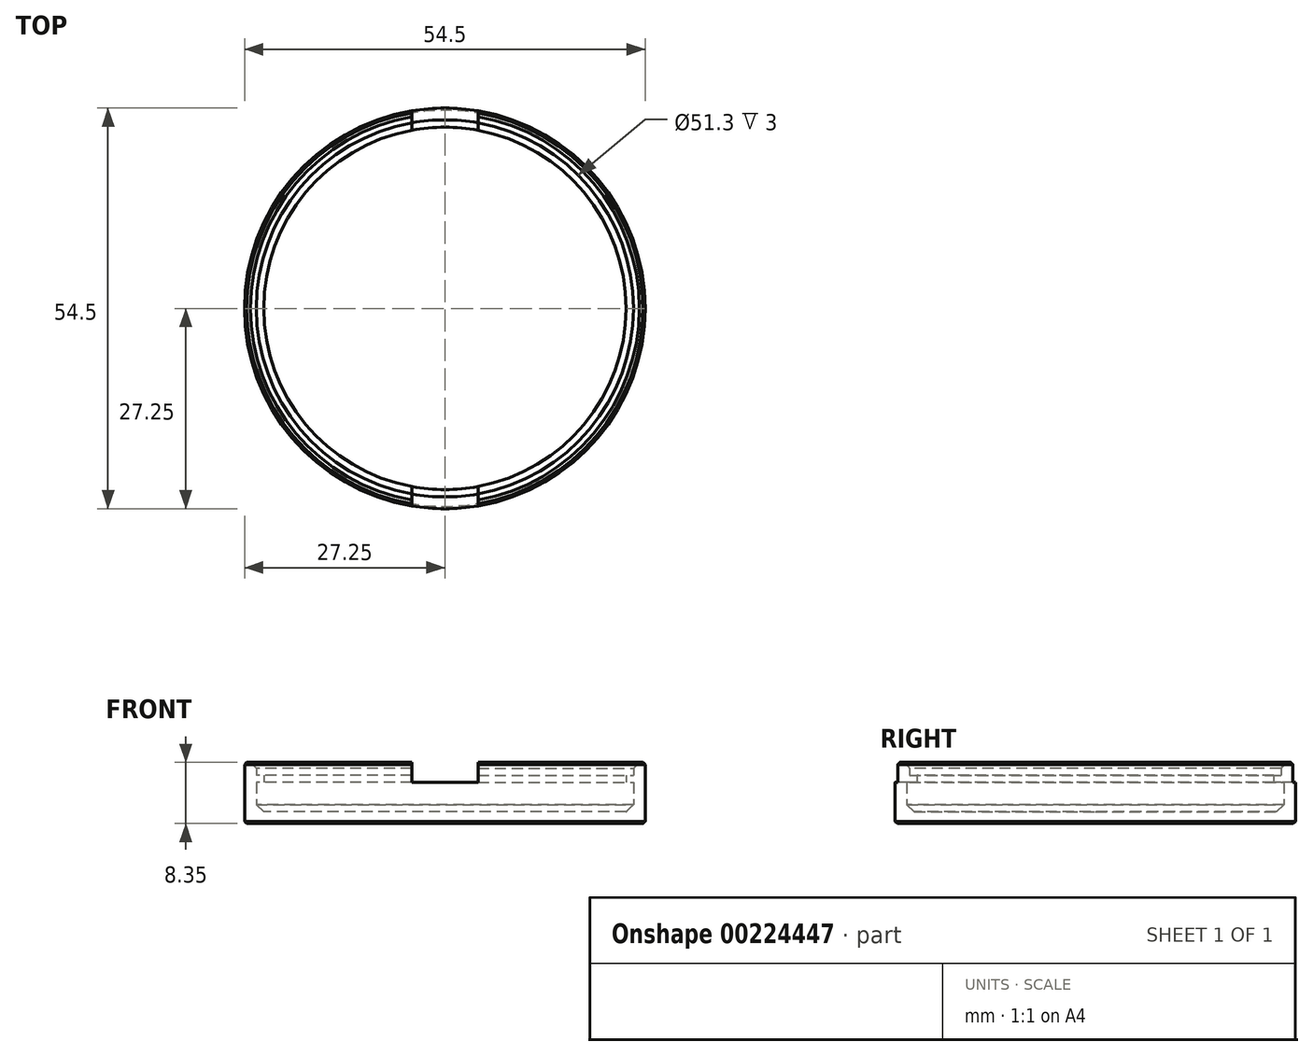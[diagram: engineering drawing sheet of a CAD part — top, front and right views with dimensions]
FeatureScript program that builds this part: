
annotation { "Feature Type Name" : "Feature", "Feature Type Description" : "" }
export const myFeature = defineFeature(function(context is Context, id is Id, definition is map)
    precondition{}
    {
        {
            assignVariable(context, id + "F0", {"name" : "_Tolerance", "anyValue" : .3});
        }
        {
            assignVariable(context, id + "F1", {"name" : "BatteryThickness", "anyValue" : 4});
        }
        {
            assignVariable(context, id + "F2", {"name" : "CPThickness", "anyValue" : 1.75});
        }
        {
            assignVariable(context, id + "F3", {"name" : "LipDepth", "anyValue" : 1});
        }
        {
            assignVariable(context, id + "F4", {"name" : "WallThickness", "anyValue" : 1.6});
        }
        {
            var Q0;
            Q0=qCreatedBy(makeId("Top.planeOp"),FACE);
            var sketch = newSketch(context, id + "F5", { "sketchPlane" : qUnion([Q0])});
            skCircle(sketch, "E0", {"center": v(0, 0) * mm, "radius": 25.65 * mm});
            skLineSegment(sketch, "E1", {"start": v(0, 25.65) * mm, "end": v(0, -25.65) * mm, "construction": true});
            skCircle(sketch, "E2.0", {"center": v(0, 0) * mm, "radius": 27.25 * mm});
            skCircle(sketch, "E3.0", {"center": v(0, 0) * mm, "radius": 24.65 * mm});
            skLineSegment(sketch, "E4", {"start": v(-4.5, 26.88) * mm, "end": v(-4.5, 24.24) * mm});
            skLineSegment(sketch, "E5.MirrorCS", {"start": v(4.5, 26.88) * mm, "end": v(4.5, 24.24) * mm});
            skLineSegment(sketch, "E6.trimOffspring", {"start": v(-4.5, -24.24) * mm, "end": v(-4.5, -26.88) * mm});
            skLineSegment(sketch, "E7.trimOffspring", {"start": v(4.5, -24.24) * mm, "end": v(4.5, -26.88) * mm});
            skSolve(sketch);
        }
        {
            var Q0;
            {var subQ0=sQuery(id+"F5.wireOp",EDGE,"E3.0");var subQ1=makeQuery(id+"F5.imprint","INTERSECT",VERTEX,{"derivedFrom":[subQ0,sQuery(id+"F5.wireOp",EDGE,"E4")]});Q0=makeQuery(id+"F5.imprint","IMPRINT",FACE,{"disambiguationData":[TD([[makeQuery(id+"F5.imprint","IMPRINT",EDGE,{"disambiguationData":[TD([[subQ1,1.0]])],"derivedFrom":subQ0}),1.0]])]});}
            extrude(context, id + "F6", {"entities" : qUnion([Q0]), "depth" : (getVariable(context, 'WallThickness') + getVariable(context, 'BatteryThickness')) * mm});
        }
        {
            var Q0;
            {var subQ0=sQuery(id+"F5.wireOp",EDGE,"E4");var subQ1=sQuery(id+"F5.wireOp",EDGE,"E0");var subQ2=makeQuery(id+"F5.imprint","INTERSECT",VERTEX,{"derivedFrom":[subQ1,subQ0]});Q0=makeQuery(id+"F5.imprint","IMPRINT",FACE,{"disambiguationData":[TD([[makeQuery(id+"F5.imprint","IMPRINT",EDGE,{"disambiguationData":[TD([[subQ2,-1.0]])],"derivedFrom":subQ1}),1.0]])]});}
            var Q1;
            {var subQ0=sQuery(id+"F5.wireOp",EDGE,"E6.trimOffspring");var subQ1=sQuery(id+"F5.wireOp",EDGE,"E0");var subQ2=makeQuery(id+"F5.imprint","INTERSECT",VERTEX,{"derivedFrom":[subQ1,subQ0]});Q1=makeQuery(id+"F5.imprint","IMPRINT",FACE,{"disambiguationData":[TD([[makeQuery(id+"F5.imprint","IMPRINT",EDGE,{"disambiguationData":[TD([[subQ2,-1.0]])],"derivedFrom":subQ1}),1.0]])]});}
            var Q2;
            {var subQ0=sQuery(id+"F5.wireOp",EDGE,"E5.MirrorCS");var subQ1=sQuery(id+"F5.wireOp",EDGE,"E0");var subQ2=makeQuery(id+"F5.imprint","INTERSECT",VERTEX,{"derivedFrom":[subQ1,subQ0]});Q2=makeQuery(id+"F5.imprint","IMPRINT",FACE,{"disambiguationData":[TD([[makeQuery(id+"F5.imprint","IMPRINT",EDGE,{"disambiguationData":[TD([[subQ2,1.0]])],"derivedFrom":subQ1}),1.0]])]});}
            var Q3;
            {var subQ0=sQuery(id+"F5.wireOp",EDGE,"E4");var subQ1=sQuery(id+"F5.wireOp",EDGE,"E0");var subQ2=makeQuery(id+"F5.imprint","INTERSECT",VERTEX,{"derivedFrom":[subQ1,subQ0]});Q3=makeQuery(id+"F5.imprint","IMPRINT",FACE,{"disambiguationData":[TD([[makeQuery(id+"F5.imprint","IMPRINT",EDGE,{"disambiguationData":[TD([[subQ2,1.0]])],"derivedFrom":subQ1}),1.0]])]});}
            extrude(context, id + "F7", {"entities" : qUnion([Q0, Q1, Q2, Q3]), "operationType" : NewBodyOperationType.ADD, "depth" : (getVariable(context, 'WallThickness') + getVariable(context, 'BatteryThickness') + getVariable(context, 'LipDepth')) * mm});
        }
        {
            var Q0;
            {var subQ0=sQuery(id+"F5.wireOp",EDGE,"E4");var subQ1=sQuery(id+"F5.wireOp",EDGE,"E0");var subQ2=makeQuery(id+"F5.imprint","INTERSECT",VERTEX,{"derivedFrom":[subQ1,subQ0]});Q0=makeQuery(id+"F5.imprint","IMPRINT",FACE,{"disambiguationData":[TD([[makeQuery(id+"F5.imprint","IMPRINT",EDGE,{"disambiguationData":[TD([[subQ2,-1.0]])],"derivedFrom":subQ1}),-1.0]])]});}
            var Q1;
            {var subQ0=sQuery(id+"F5.wireOp",EDGE,"E6.trimOffspring");var subQ1=sQuery(id+"F5.wireOp",EDGE,"E0");var subQ2=makeQuery(id+"F5.imprint","INTERSECT",VERTEX,{"derivedFrom":[subQ1,subQ0]});Q1=makeQuery(id+"F5.imprint","IMPRINT",FACE,{"disambiguationData":[TD([[makeQuery(id+"F5.imprint","IMPRINT",EDGE,{"disambiguationData":[TD([[subQ2,-1.0]])],"derivedFrom":subQ1}),-1.0]])]});}
            var Q2;
            {var subQ0=sQuery(id+"F5.wireOp",EDGE,"E5.MirrorCS");var subQ1=sQuery(id+"F5.wireOp",EDGE,"E0");var subQ2=makeQuery(id+"F5.imprint","INTERSECT",VERTEX,{"derivedFrom":[subQ1,subQ0]});Q2=makeQuery(id+"F5.imprint","IMPRINT",FACE,{"disambiguationData":[TD([[makeQuery(id+"F5.imprint","IMPRINT",EDGE,{"disambiguationData":[TD([[subQ2,1.0]])],"derivedFrom":subQ1}),-1.0]])]});}
            var Q3;
            {var subQ0=sQuery(id+"F5.wireOp",EDGE,"E4");var subQ1=sQuery(id+"F5.wireOp",EDGE,"E0");var subQ2=makeQuery(id+"F5.imprint","INTERSECT",VERTEX,{"derivedFrom":[subQ1,subQ0]});Q3=makeQuery(id+"F5.imprint","IMPRINT",FACE,{"disambiguationData":[TD([[makeQuery(id+"F5.imprint","IMPRINT",EDGE,{"disambiguationData":[TD([[subQ2,1.0]])],"derivedFrom":subQ1}),-1.0]])]});}
            extrude(context, id + "F8", {"entities" : qUnion([Q0, Q1, Q2, Q3]), "operationType" : NewBodyOperationType.ADD, "depth" : (getVariable(context, 'WallThickness') + getVariable(context, 'BatteryThickness') + getVariable(context, 'LipDepth') + getVariable(context, 'CPThickness')) * mm});
        }
        {
            var Q0;
            {var subQ0=sQuery(id+"F5.wireOp",EDGE,"E6.trimOffspring");var subQ1=sQuery(id+"F5.wireOp",EDGE,"E0");var subQ2=makeQuery(id+"F5.imprint","INTERSECT",VERTEX,{"derivedFrom":[subQ1,subQ0]});Q0=makeQuery(id+"F5.imprint","IMPRINT",FACE,{"disambiguationData":[TD([[makeQuery(id+"F5.imprint","IMPRINT",EDGE,{"disambiguationData":[TD([[subQ2,-1.0]])],"derivedFrom":subQ1}),-1.0]])]});}
            var Q1;
            {var subQ0=sQuery(id+"F5.wireOp",EDGE,"E5.MirrorCS");var subQ1=sQuery(id+"F5.wireOp",EDGE,"E0");var subQ2=makeQuery(id+"F5.imprint","INTERSECT",VERTEX,{"derivedFrom":[subQ1,subQ0]});Q1=makeQuery(id+"F5.imprint","IMPRINT",FACE,{"disambiguationData":[TD([[makeQuery(id+"F5.imprint","IMPRINT",EDGE,{"disambiguationData":[TD([[subQ2,-1.0]])],"derivedFrom":subQ1}),-1.0]])]});}
            var Q2;
            {var subQ0=sQuery(id+"F5.wireOp",EDGE,"E6.trimOffspring");var subQ1=sQuery(id+"F5.wireOp",EDGE,"E0");var subQ2=makeQuery(id+"F5.imprint","INTERSECT",VERTEX,{"derivedFrom":[subQ1,subQ0]});Q2=makeQuery(id+"F5.imprint","IMPRINT",FACE,{"disambiguationData":[TD([[makeQuery(id+"F5.imprint","IMPRINT",EDGE,{"disambiguationData":[TD([[subQ2,-1.0]])],"derivedFrom":subQ1}),1.0]])]});}
            var Q3;
            {var subQ0=sQuery(id+"F5.wireOp",EDGE,"E4");var subQ1=sQuery(id+"F5.wireOp",EDGE,"E0");var subQ2=makeQuery(id+"F5.imprint","INTERSECT",VERTEX,{"derivedFrom":[subQ1,subQ0]});Q3=makeQuery(id+"F5.imprint","IMPRINT",FACE,{"disambiguationData":[TD([[makeQuery(id+"F5.imprint","IMPRINT",EDGE,{"disambiguationData":[TD([[subQ2,1.0]])],"derivedFrom":subQ1}),1.0]])]});}
            extrude(context, id + "F9", {"entities" : qUnion([Q0, Q1, Q2, Q3]), "operationType" : NewBodyOperationType.REMOVE, "depth" : (getVariable(context, 'WallThickness') + getVariable(context, 'BatteryThickness') + getVariable(context, 'LipDepth') + getVariable(context, 'CPThickness')) * mm, "hasSecondDirection" : true, "secondDirectionOppositeDirection" : false, "secondDirectionDepth" : (getVariable(context, 'WallThickness') + getVariable(context, 'BatteryThickness')) * mm});
        }
        {
            var Q0;
            {var subQ0=sQuery(id+"F5.wireOp",EDGE,"E3.0");var subQ1=sQuery(id+"F5.wireOp",EDGE,"E2.0");Q0=makeQuery(id+"F9.boolean.opBoolean","MERGE",FACE,{"derivedFrom":[makeQuery(id+"F6.opExtrude","CAP_FACE",FACE,{"disambiguationData":[OSD([subQ0])],"isStart":false}),makeQuery(id+"F9.opExtrude","CAP_FACE",FACE,{"disambiguationData":[OSD([subQ1,subQ0,sQuery(id+"F5.wireOp",EDGE,"E4"),sQuery(id+"F5.wireOp",EDGE,"E5.MirrorCS")])],"isStart":true}),makeQuery(id+"F9.opExtrude","CAP_FACE",FACE,{"disambiguationData":[OSD([subQ1,subQ0,sQuery(id+"F5.wireOp",EDGE,"E6.trimOffspring"),sQuery(id+"F5.wireOp",EDGE,"E7.trimOffspring")])],"isStart":true})]});}
            shell(context, id + "F10", {"entities" : qUnion([Q0]), "thickness" : (getVariable(context, 'WallThickness')) * mm});
        }
        {
            var Q0;
            {var subQ0=sQuery(id+"F5.wireOp",EDGE,"E2.0");Q0=makeQuery(id+"F10.opShell","OFFSET_EDGE",EDGE,{"disambiguationData":[OSD([subQ0]),TDD([makeQuery(id+"F9.boolean.opBoolean","COPY",EDGE,{"derivedFrom":makeQuery(id+"F9.opExtrude","CAP_EDGE",EDGE,{"disambiguationData":[OSD([subQ0]),TDD([makeQuery(id+"F5.imprint","IMPRINT",EDGE,{"disambiguationData":[TD([[makeQuery(id+"F5.imprint","INTERSECT",VERTEX,{"derivedFrom":[subQ0,sQuery(id+"F5.wireOp",EDGE,"E4")]}),1.0]])],"derivedFrom":subQ0})])],"isStart":true})}),makeQuery(id+"F9.boolean.opBoolean","COPY",EDGE,{"derivedFrom":makeQuery(id+"F9.opExtrude","CAP_EDGE",EDGE,{"disambiguationData":[OSD([subQ0]),TDD([makeQuery(id+"F5.imprint","IMPRINT",EDGE,{"disambiguationData":[TD([[makeQuery(id+"F5.imprint","INTERSECT",VERTEX,{"derivedFrom":[subQ0,sQuery(id+"F5.wireOp",EDGE,"E6.trimOffspring")]}),-1.0]])],"derivedFrom":subQ0})])],"isStart":true})})]),OD(2.0)]});}
            var Q1;
            {var subQ0=sQuery(id+"F5.wireOp",EDGE,"E2.0");Q1=makeQuery(id+"F10.opShell","OFFSET_EDGE",EDGE,{"disambiguationData":[OSD([subQ0]),TDD([makeQuery(id+"F9.boolean.opBoolean","COPY",EDGE,{"derivedFrom":makeQuery(id+"F9.opExtrude","CAP_EDGE",EDGE,{"disambiguationData":[OSD([subQ0]),TDD([makeQuery(id+"F5.imprint","IMPRINT",EDGE,{"disambiguationData":[TD([[makeQuery(id+"F5.imprint","INTERSECT",VERTEX,{"derivedFrom":[subQ0,sQuery(id+"F5.wireOp",EDGE,"E4")]}),1.0]])],"derivedFrom":subQ0})])],"isStart":true})}),makeQuery(id+"F9.boolean.opBoolean","COPY",EDGE,{"derivedFrom":makeQuery(id+"F9.opExtrude","CAP_EDGE",EDGE,{"disambiguationData":[OSD([subQ0]),TDD([makeQuery(id+"F5.imprint","IMPRINT",EDGE,{"disambiguationData":[TD([[makeQuery(id+"F5.imprint","INTERSECT",VERTEX,{"derivedFrom":[subQ0,sQuery(id+"F5.wireOp",EDGE,"E6.trimOffspring")]}),-1.0]])],"derivedFrom":subQ0})])],"isStart":true})})]),OD(3.0)]});}
            chamfer(context, id + "F11", {"entities" : qUnion([Q0, Q1]), "width" : (getVariable(context, 'LipDepth')) * mm, "tangentPropagation" : true});
        }
        {
            var Q0;
            {var subQ0=sQuery(id+"F5.wireOp",EDGE,"E0");Q0=makeQuery(id+"F9.boolean.opBoolean","SPLIT",EDGE,{"disambiguationData":[TD([makeQuery(id+"F9.opExtrude","SWEPT_FACE",FACE,{"disambiguationData":[OSD([sQuery(id+"F5.wireOp",EDGE,"E4")])]})])],"derivedFrom":makeQuery(id+"F8.opExtrude","CAP_EDGE",EDGE,{"disambiguationData":[OSD([subQ0])],"isStart":false})});}
            var Q1;
            {var subQ0=sQuery(id+"F5.wireOp",EDGE,"E0");Q1=makeQuery(id+"F9.boolean.opBoolean","SPLIT",EDGE,{"disambiguationData":[TD([makeQuery(id+"F9.opExtrude","SWEPT_FACE",FACE,{"disambiguationData":[OSD([sQuery(id+"F5.wireOp",EDGE,"E5.MirrorCS")])]})])],"derivedFrom":makeQuery(id+"F8.opExtrude","CAP_EDGE",EDGE,{"disambiguationData":[OSD([subQ0])],"isStart":false})});}
            chamfer(context, id + "F12", {"entities" : qUnion([Q0, Q1]), "width" : (getVariable(context, 'WallThickness') / 2) * mm, "tangentPropagation" : true});
        }
        {
            var Q0;
            {var subQ0=sQuery(id+"F5.wireOp",EDGE,"E0");var subQ1=sQuery(id+"F5.wireOp",EDGE,"E3.0");Q0=makeQuery(id+"F8.boolean.opBoolean","MERGE",FACE,{"derivedFrom":[makeQuery(id+"F7.boolean.opBoolean","MERGE",FACE,{"derivedFrom":[makeQuery(id+"F6.opExtrude","CAP_FACE",FACE,{"disambiguationData":[OSD([subQ1])],"isStart":true}),makeQuery(id+"F7.opExtrude","CAP_FACE",FACE,{"disambiguationData":[OSD([subQ0,subQ1])],"isStart":true})]}),makeQuery(id+"F8.opExtrude","CAP_FACE",FACE,{"disambiguationData":[OSD([subQ0,sQuery(id+"F5.wireOp",EDGE,"E2.0")])],"isStart":true})]});}
            var Q1;
            {var subQ0=sQuery(id+"F5.wireOp",EDGE,"E2.0");Q1=makeQuery(id+"F9.boolean.opBoolean","SPLIT",EDGE,{"disambiguationData":[TD([makeQuery(id+"F9.opExtrude","SWEPT_FACE",FACE,{"disambiguationData":[OSD([sQuery(id+"F5.wireOp",EDGE,"E4")])]})])],"derivedFrom":makeQuery(id+"F8.opExtrude","CAP_EDGE",EDGE,{"disambiguationData":[OSD([subQ0])],"isStart":false})});}
            var Q2;
            {var subQ0=sQuery(id+"F5.wireOp",EDGE,"E2.0");Q2=makeQuery(id+"F9.boolean.opBoolean","SPLIT",EDGE,{"disambiguationData":[TD([makeQuery(id+"F9.opExtrude","SWEPT_FACE",FACE,{"disambiguationData":[OSD([sQuery(id+"F5.wireOp",EDGE,"E5.MirrorCS")])]})])],"derivedFrom":makeQuery(id+"F8.opExtrude","CAP_EDGE",EDGE,{"disambiguationData":[OSD([subQ0])],"isStart":false})});}
            chamfer(context, id + "F13", {"entities" : qUnion([Q0, Q1, Q2]), "width" : (getVariable(context, '_Tolerance')) * mm, "tangentPropagation" : true});
        }
    });
